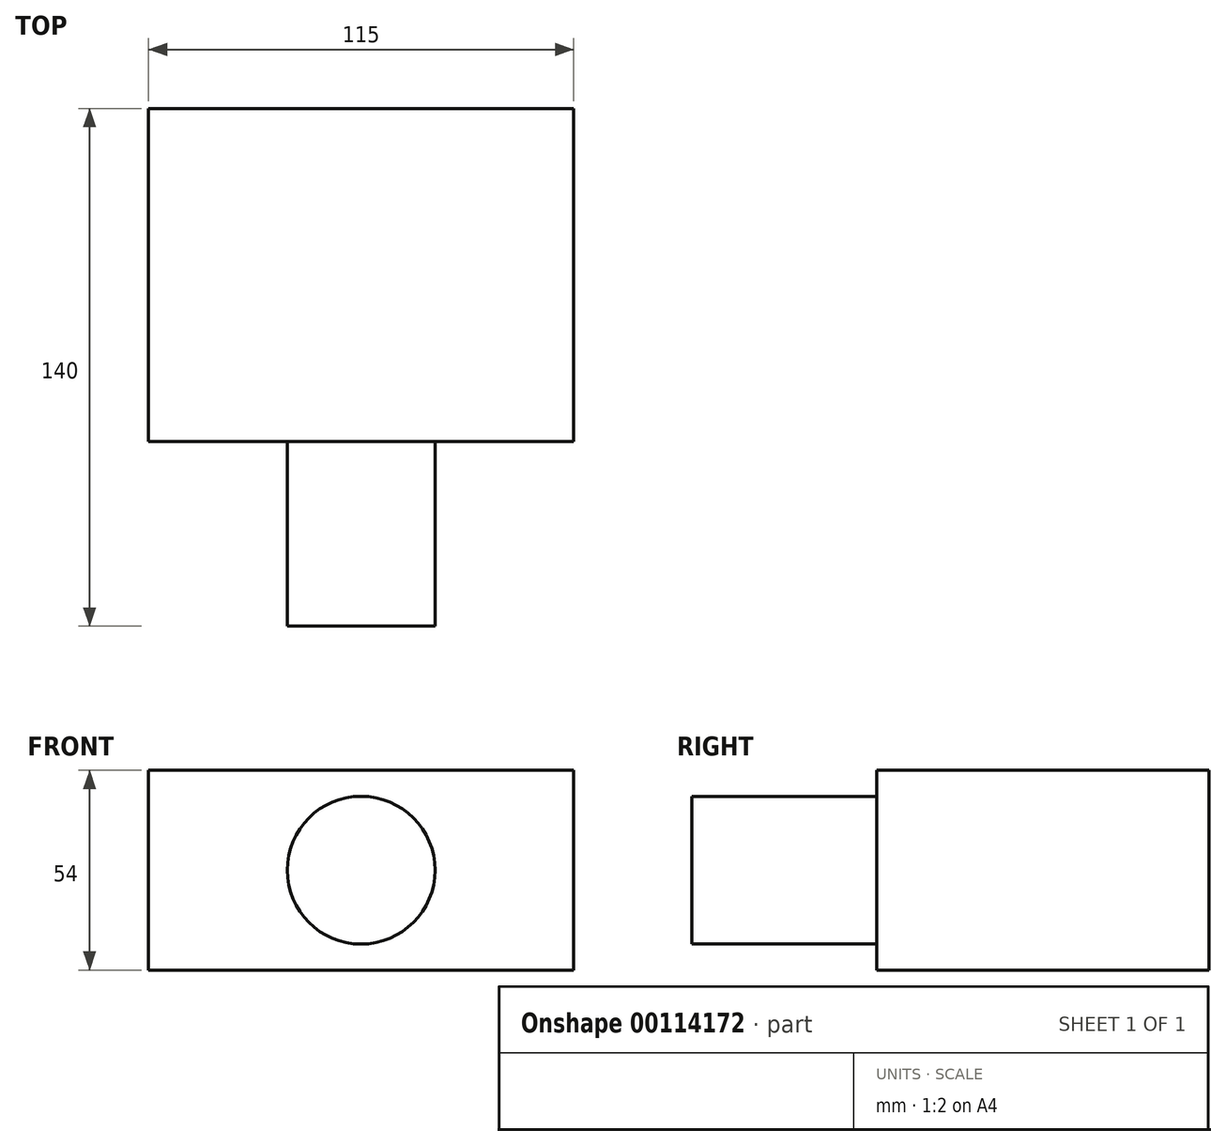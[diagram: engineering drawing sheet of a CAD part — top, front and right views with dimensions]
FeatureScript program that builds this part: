
annotation { "Feature Type Name" : "Feature", "Feature Type Description" : "" }
export const myFeature = defineFeature(function(context is Context, id is Id, definition is map)
    precondition{}
    {
        {
            var Q0;
            Q0=qCreatedBy(makeId("Top.planeOp"),FACE);
            var sketch = newSketch(context, id + "F0", { "sketchPlane" : qUnion([Q0])});
            skLineSegment(sketch, "E0.bottom", {"start": v(57.5, 45) * mm, "end": v(-57.5, 45) * mm});
            skLineSegment(sketch, "E0.top", {"start": v(57.5, -45) * mm, "end": v(-57.5, -45) * mm});
            skLineSegment(sketch, "E0.left", {"start": v(57.5, 45) * mm, "end": v(57.5, -45) * mm});
            skLineSegment(sketch, "E0.right", {"start": v(-57.5, 45) * mm, "end": v(-57.5, -45) * mm});
            skPoint(sketch, "E0.middle", {"position": v(0, 0) * mm});
            skSolve(sketch);
        }
        {
            var Q0;
            Q0=makeQuery(id+"F0.imprint","IMPRINT",FACE,{"disambiguationData":[TD([[makeQuery(id+"F0.imprint","IMPRINT",EDGE,{"derivedFrom":sQuery(id+"F0.wireOp",EDGE,"E0.bottom")}),1.0]])]});
            extrude(context, id + "F1", {"entities" : qUnion([Q0]), "depth" : 54 * mm});
        }
        {
            var Q0;
            Q0=makeQuery(id+"F1.opExtrude","SWEPT_FACE",FACE,{"disambiguationData":[OSD([sQuery(id+"F0.wireOp",EDGE,"E0.top")])]});
            var sketch = newSketch(context, id + "F2", { "sketchPlane" : qUnion([Q0])});
            skCircle(sketch, "E1", {"center": v(0, 27) * mm, "radius": 20 * mm});
            skLineSegment(sketch, "E2", {"start": v(0, 27) * mm, "end": v(0, 0) * mm});
            skSolve(sketch);
        }
        {
            var Q0;
            Q0=makeQuery(id+"F2.imprint","IMPRINT",FACE,{"disambiguationData":[TD([[makeQuery(id+"F2.imprint","IMPRINT",EDGE,{"derivedFrom":sQuery(id+"F2.wireOp",EDGE,"E1")}),1.0]])]});
            extrude(context, id + "F3", {"entities" : qUnion([Q0]), "depth" : 50 * mm});
        }
    });
